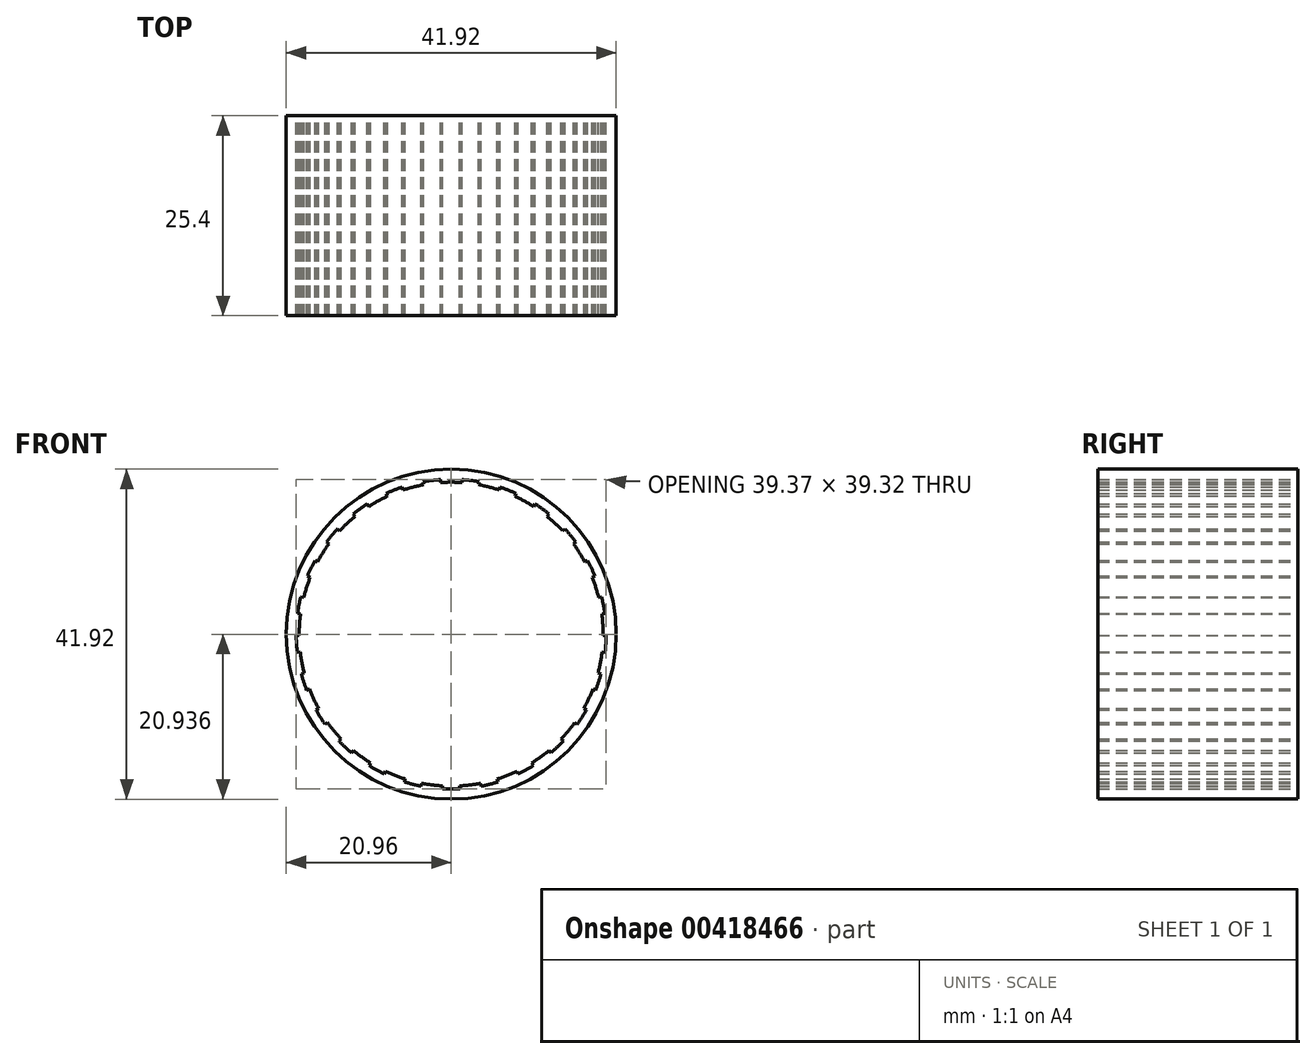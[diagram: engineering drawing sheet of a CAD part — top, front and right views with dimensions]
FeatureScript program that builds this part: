
annotation { "Feature Type Name" : "Feature", "Feature Type Description" : "" }
export const myFeature = defineFeature(function(context is Context, id is Id, definition is map)
    precondition{}
    {
        {
            var Q0;
            Q0=qCreatedBy(makeId("Front.planeOp"),FACE);
            var sketch = newSketch(context, id + "F0", { "sketchPlane" : qUnion([Q0])});
            skCircle(sketch, "E0", {"center": v(0, 0) * mm, "radius": 20.96 * mm});
            skLineSegment(sketch, "E1", {"start": v(1.38, 19.64) * mm, "end": v(1.35, 19.26) * mm});
            skLineSegment(sketch, "E2", {"start": v(-1.38, 19.64) * mm, "end": v(-1.35, 19.26) * mm});
            skArc(sketch, "E3", {"start": v(1.35, 19.26) * mm, "mid": v(0, 19.3) * mm, "end": v(-1.35, 19.26) * mm});
            skPoint(sketch, "E4", {"position": v(1.35, 19.26) * mm});
            skPoint(sketch, "E5", {"position": v(-1.35, 19.26) * mm});
            skPoint(sketch, "E6", {"position": v(0, 19.3) * mm});
            skCircle(sketch, "E7", {"center": v(0, 0) * mm, "radius": 19.69 * mm});
            skArc(sketch, "E8.1.0", {"start": v(-3.48, 18.99) * mm, "mid": v(-4.8, 18.7) * mm, "end": v(-6.1, 18.32) * mm});
            skLineSegment(sketch, "E8.1.1", {"start": v(-3.55, 19.36) * mm, "end": v(-3.48, 18.99) * mm});
            skLineSegment(sketch, "E8.1.2", {"start": v(-6.22, 18.68) * mm, "end": v(-6.1, 18.32) * mm});
            skArc(sketch, "E8.2.0", {"start": v(-8.1, 17.52) * mm, "mid": v(-9.3, 16.92) * mm, "end": v(-10.46, 16.23) * mm});
            skLineSegment(sketch, "E8.2.1", {"start": v(-8.26, 17.87) * mm, "end": v(-8.1, 17.52) * mm});
            skLineSegment(sketch, "E8.2.2", {"start": v(-10.67, 16.55) * mm, "end": v(-10.46, 16.23) * mm});
            skArc(sketch, "E8.3.0", {"start": v(-12.2, 14.96) * mm, "mid": v(-13.21, 14.07) * mm, "end": v(-14.17, 13.11) * mm});
            skLineSegment(sketch, "E8.3.1", {"start": v(-12.44, 15.26) * mm, "end": v(-12.2, 14.96) * mm});
            skLineSegment(sketch, "E8.3.2", {"start": v(-14.44, 13.37) * mm, "end": v(-14.17, 13.11) * mm});
            skArc(sketch, "E8.4.0", {"start": v(-15.54, 11.46) * mm, "mid": v(-16.3, 10.34) * mm, "end": v(-16.98, 9.18) * mm});
            skLineSegment(sketch, "E8.4.1", {"start": v(-15.84, 11.68) * mm, "end": v(-15.54, 11.46) * mm});
            skLineSegment(sketch, "E8.4.2", {"start": v(-17.32, 9.36) * mm, "end": v(-16.98, 9.18) * mm});
            skArc(sketch, "E8.5.0", {"start": v(-17.9, 7.23) * mm, "mid": v(-18.36, 5.97) * mm, "end": v(-18.73, 4.67) * mm});
            skLineSegment(sketch, "E8.5.1", {"start": v(-18.25, 7.38) * mm, "end": v(-17.9, 7.23) * mm});
            skLineSegment(sketch, "E8.5.2", {"start": v(-19.1, 4.76) * mm, "end": v(-18.73, 4.67) * mm});
            skArc(sketch, "E8.6.0", {"start": v(-19.13, 2.56) * mm, "mid": v(-19.27, 1.21) * mm, "end": v(-19.3, -0.14) * mm});
            skLineSegment(sketch, "E8.6.1", {"start": v(-19.51, 2.6) * mm, "end": v(-19.13, 2.56) * mm});
            skLineSegment(sketch, "E8.6.2", {"start": v(-19.68, -0.14) * mm, "end": v(-19.3, -0.14) * mm});
            skArc(sketch, "E8.7.0", {"start": v(-19.17, -2.28) * mm, "mid": v(-18.96, -3.62) * mm, "end": v(-18.66, -4.93) * mm});
            skLineSegment(sketch, "E8.7.1", {"start": v(-19.55, -2.33) * mm, "end": v(-19.17, -2.28) * mm});
            skLineSegment(sketch, "E8.7.2", {"start": v(-19.03, -5.03) * mm, "end": v(-18.66, -4.93) * mm});
            skArc(sketch, "E8.8.0", {"start": v(-18, -6.98) * mm, "mid": v(-17.47, -8.22) * mm, "end": v(-16.85, -9.42) * mm});
            skLineSegment(sketch, "E8.8.1", {"start": v(-18.35, -7.12) * mm, "end": v(-18, -6.98) * mm});
            skLineSegment(sketch, "E8.8.2", {"start": v(-17.18, -9.6) * mm, "end": v(-16.85, -9.42) * mm});
            skArc(sketch, "E8.9.0", {"start": v(-15.7, -11.24) * mm, "mid": v(-14.87, -12.3) * mm, "end": v(-13.98, -13.31) * mm});
            skLineSegment(sketch, "E8.9.1", {"start": v(-16, -11.46) * mm, "end": v(-15.7, -11.24) * mm});
            skLineSegment(sketch, "E8.9.2", {"start": v(-14.25, -13.58) * mm, "end": v(-13.98, -13.31) * mm});
            skArc(sketch, "E8.10.0", {"start": v(-12.4, -14.79) * mm, "mid": v(-11.35, -15.62) * mm, "end": v(-10.23, -16.37) * mm});
            skLineSegment(sketch, "E8.10.1", {"start": v(-12.65, -15.08) * mm, "end": v(-12.4, -14.79) * mm});
            skLineSegment(sketch, "E8.10.2", {"start": v(-10.43, -16.7) * mm, "end": v(-10.23, -16.37) * mm});
            skArc(sketch, "E8.11.0", {"start": v(-8.34, -17.4) * mm, "mid": v(-7.1, -17.95) * mm, "end": v(-5.84, -18.4) * mm});
            skLineSegment(sketch, "E8.11.1", {"start": v(-8.5, -17.75) * mm, "end": v(-8.34, -17.4) * mm});
            skLineSegment(sketch, "E8.11.2", {"start": v(-5.95, -18.76) * mm, "end": v(-5.84, -18.4) * mm});
            skArc(sketch, "E8.12.0", {"start": v(-3.75, -18.94) * mm, "mid": v(-2.42, -19.15) * mm, "end": v(-1.08, -19.27) * mm});
            skLineSegment(sketch, "E8.12.1", {"start": v(-3.83, -19.3) * mm, "end": v(-3.75, -18.94) * mm});
            skLineSegment(sketch, "E8.12.2", {"start": v(-1.1, -19.65) * mm, "end": v(-1.08, -19.27) * mm});
            skArc(sketch, "E8.13.0", {"start": v(1.08, -19.27) * mm, "mid": v(2.42, -19.15) * mm, "end": v(3.75, -18.94) * mm});
            skLineSegment(sketch, "E8.13.1", {"start": v(1.1, -19.65) * mm, "end": v(1.08, -19.27) * mm});
            skLineSegment(sketch, "E8.13.2", {"start": v(3.83, -19.3) * mm, "end": v(3.75, -18.94) * mm});
            skArc(sketch, "E8.14.0", {"start": v(5.84, -18.4) * mm, "mid": v(7.1, -17.95) * mm, "end": v(8.34, -17.4) * mm});
            skLineSegment(sketch, "E8.14.1", {"start": v(5.95, -18.76) * mm, "end": v(5.84, -18.4) * mm});
            skLineSegment(sketch, "E8.14.2", {"start": v(8.5, -17.75) * mm, "end": v(8.34, -17.4) * mm});
            skArc(sketch, "E8.15.0", {"start": v(10.23, -16.37) * mm, "mid": v(11.35, -15.62) * mm, "end": v(12.4, -14.79) * mm});
            skLineSegment(sketch, "E8.15.1", {"start": v(10.43, -16.7) * mm, "end": v(10.23, -16.37) * mm});
            skLineSegment(sketch, "E8.15.2", {"start": v(12.65, -15.08) * mm, "end": v(12.4, -14.79) * mm});
            skArc(sketch, "E8.16.0", {"start": v(13.98, -13.31) * mm, "mid": v(14.87, -12.3) * mm, "end": v(15.7, -11.24) * mm});
            skLineSegment(sketch, "E8.16.1", {"start": v(14.25, -13.58) * mm, "end": v(13.98, -13.31) * mm});
            skLineSegment(sketch, "E8.16.2", {"start": v(16, -11.46) * mm, "end": v(15.7, -11.24) * mm});
            skArc(sketch, "E8.17.0", {"start": v(16.85, -9.42) * mm, "mid": v(17.47, -8.22) * mm, "end": v(18, -6.98) * mm});
            skLineSegment(sketch, "E8.17.1", {"start": v(17.18, -9.6) * mm, "end": v(16.85, -9.42) * mm});
            skLineSegment(sketch, "E8.17.2", {"start": v(18.35, -7.12) * mm, "end": v(18, -6.98) * mm});
            skArc(sketch, "E8.18.0", {"start": v(18.66, -4.93) * mm, "mid": v(18.96, -3.62) * mm, "end": v(19.17, -2.28) * mm});
            skLineSegment(sketch, "E8.18.1", {"start": v(19.03, -5.03) * mm, "end": v(18.66, -4.93) * mm});
            skLineSegment(sketch, "E8.18.2", {"start": v(19.55, -2.33) * mm, "end": v(19.17, -2.28) * mm});
            skArc(sketch, "E8.19.0", {"start": v(19.3, -0.14) * mm, "mid": v(19.27, 1.21) * mm, "end": v(19.13, 2.56) * mm});
            skLineSegment(sketch, "E8.19.1", {"start": v(19.68, -0.14) * mm, "end": v(19.3, -0.14) * mm});
            skLineSegment(sketch, "E8.19.2", {"start": v(19.51, 2.6) * mm, "end": v(19.13, 2.56) * mm});
            skArc(sketch, "E8.20.0", {"start": v(18.73, 4.67) * mm, "mid": v(18.36, 5.97) * mm, "end": v(17.9, 7.23) * mm});
            skLineSegment(sketch, "E8.20.1", {"start": v(19.1, 4.76) * mm, "end": v(18.73, 4.67) * mm});
            skLineSegment(sketch, "E8.20.2", {"start": v(18.25, 7.38) * mm, "end": v(17.9, 7.23) * mm});
            skArc(sketch, "E8.21.0", {"start": v(16.98, 9.18) * mm, "mid": v(16.3, 10.34) * mm, "end": v(15.54, 11.46) * mm});
            skLineSegment(sketch, "E8.21.1", {"start": v(17.32, 9.36) * mm, "end": v(16.98, 9.18) * mm});
            skLineSegment(sketch, "E8.21.2", {"start": v(15.84, 11.68) * mm, "end": v(15.54, 11.46) * mm});
            skArc(sketch, "E8.22.0", {"start": v(14.17, 13.11) * mm, "mid": v(13.21, 14.07) * mm, "end": v(12.2, 14.96) * mm});
            skLineSegment(sketch, "E8.22.1", {"start": v(14.44, 13.37) * mm, "end": v(14.17, 13.11) * mm});
            skLineSegment(sketch, "E8.22.2", {"start": v(12.44, 15.26) * mm, "end": v(12.2, 14.96) * mm});
            skArc(sketch, "E8.23.0", {"start": v(10.46, 16.23) * mm, "mid": v(9.3, 16.92) * mm, "end": v(8.1, 17.52) * mm});
            skLineSegment(sketch, "E8.23.1", {"start": v(10.67, 16.55) * mm, "end": v(10.46, 16.23) * mm});
            skLineSegment(sketch, "E8.23.2", {"start": v(8.26, 17.87) * mm, "end": v(8.1, 17.52) * mm});
            skArc(sketch, "E8.24.0", {"start": v(6.1, 18.32) * mm, "mid": v(4.8, 18.7) * mm, "end": v(3.48, 18.99) * mm});
            skLineSegment(sketch, "E8.24.1", {"start": v(6.22, 18.68) * mm, "end": v(6.1, 18.32) * mm});
            skLineSegment(sketch, "E8.24.2", {"start": v(3.55, 19.36) * mm, "end": v(3.48, 18.99) * mm});
            skSolve(sketch);
        }
        {
            var Q0;
            Q0 = qSketchRegion(id + "F0", true);
            extrude(context, id + "F1", {"entities" : qUnion([Q0]), "depth" : 25.4 * mm});
        }
        {
            var Q0;
            {var subQ0=sQuery(id+"F0.wireOp",EDGE,"E1");Q0=makeQuery(id+"F0.imprint","IMPRINT",FACE,{"disambiguationData":[TD([[makeQuery(id+"F0.imprint","IMPRINT",EDGE,{"derivedFrom":subQ0}),-1.0]])]});}
            var Q1;
            Q1=makeQuery(id+"F0.imprint","IMPRINT",FACE,{"disambiguationData":[TD([[makeQuery(id+"F0.imprint","IMPRINT",EDGE,{"derivedFrom":sQuery(id+"F0.wireOp",EDGE,"E8.1.0")}),-1.0]])]});
            var Q2;
            Q2=makeQuery(id+"F0.imprint","IMPRINT",FACE,{"disambiguationData":[TD([[makeQuery(id+"F0.imprint","IMPRINT",EDGE,{"derivedFrom":sQuery(id+"F0.wireOp",EDGE,"E8.2.0")}),-1.0]])]});
            var Q3;
            Q3=makeQuery(id+"F0.imprint","IMPRINT",FACE,{"disambiguationData":[TD([[makeQuery(id+"F0.imprint","IMPRINT",EDGE,{"derivedFrom":sQuery(id+"F0.wireOp",EDGE,"E8.3.0")}),-1.0]])]});
            var Q4;
            Q4=makeQuery(id+"F0.imprint","IMPRINT",FACE,{"disambiguationData":[TD([[makeQuery(id+"F0.imprint","IMPRINT",EDGE,{"derivedFrom":sQuery(id+"F0.wireOp",EDGE,"E8.4.0")}),-1.0]])]});
            var Q5;
            Q5=makeQuery(id+"F0.imprint","IMPRINT",FACE,{"disambiguationData":[TD([[makeQuery(id+"F0.imprint","IMPRINT",EDGE,{"derivedFrom":sQuery(id+"F0.wireOp",EDGE,"E8.5.0")}),-1.0]])]});
            var Q6;
            Q6=makeQuery(id+"F0.imprint","IMPRINT",FACE,{"disambiguationData":[TD([[makeQuery(id+"F0.imprint","IMPRINT",EDGE,{"derivedFrom":sQuery(id+"F0.wireOp",EDGE,"E8.6.0")}),-1.0]])]});
            var Q7;
            Q7=makeQuery(id+"F0.imprint","IMPRINT",FACE,{"disambiguationData":[TD([[makeQuery(id+"F0.imprint","IMPRINT",EDGE,{"derivedFrom":sQuery(id+"F0.wireOp",EDGE,"E8.7.0")}),-1.0]])]});
            var Q8;
            Q8=makeQuery(id+"F0.imprint","IMPRINT",FACE,{"disambiguationData":[TD([[makeQuery(id+"F0.imprint","IMPRINT",EDGE,{"derivedFrom":sQuery(id+"F0.wireOp",EDGE,"E8.8.0")}),-1.0]])]});
            var Q9;
            Q9=makeQuery(id+"F0.imprint","IMPRINT",FACE,{"disambiguationData":[TD([[makeQuery(id+"F0.imprint","IMPRINT",EDGE,{"derivedFrom":sQuery(id+"F0.wireOp",EDGE,"E8.9.0")}),-1.0]])]});
            var Q10;
            Q10=makeQuery(id+"F0.imprint","IMPRINT",FACE,{"disambiguationData":[TD([[makeQuery(id+"F0.imprint","IMPRINT",EDGE,{"derivedFrom":sQuery(id+"F0.wireOp",EDGE,"E8.10.0")}),-1.0]])]});
            var Q11;
            Q11=makeQuery(id+"F0.imprint","IMPRINT",FACE,{"disambiguationData":[TD([[makeQuery(id+"F0.imprint","IMPRINT",EDGE,{"derivedFrom":sQuery(id+"F0.wireOp",EDGE,"E8.11.0")}),-1.0]])]});
            var Q12;
            Q12=makeQuery(id+"F0.imprint","IMPRINT",FACE,{"disambiguationData":[TD([[makeQuery(id+"F0.imprint","IMPRINT",EDGE,{"derivedFrom":sQuery(id+"F0.wireOp",EDGE,"E8.12.0")}),-1.0]])]});
            var Q13;
            Q13=makeQuery(id+"F0.imprint","IMPRINT",FACE,{"disambiguationData":[TD([[makeQuery(id+"F0.imprint","IMPRINT",EDGE,{"derivedFrom":sQuery(id+"F0.wireOp",EDGE,"E8.13.0")}),-1.0]])]});
            var Q14;
            Q14=makeQuery(id+"F0.imprint","IMPRINT",FACE,{"disambiguationData":[TD([[makeQuery(id+"F0.imprint","IMPRINT",EDGE,{"derivedFrom":sQuery(id+"F0.wireOp",EDGE,"E8.14.0")}),-1.0]])]});
            var Q15;
            Q15=makeQuery(id+"F0.imprint","IMPRINT",FACE,{"disambiguationData":[TD([[makeQuery(id+"F0.imprint","IMPRINT",EDGE,{"derivedFrom":sQuery(id+"F0.wireOp",EDGE,"E8.15.0")}),-1.0]])]});
            var Q16;
            Q16=makeQuery(id+"F0.imprint","IMPRINT",FACE,{"disambiguationData":[TD([[makeQuery(id+"F0.imprint","IMPRINT",EDGE,{"derivedFrom":sQuery(id+"F0.wireOp",EDGE,"E8.16.0")}),-1.0]])]});
            var Q17;
            Q17=makeQuery(id+"F0.imprint","IMPRINT",FACE,{"disambiguationData":[TD([[makeQuery(id+"F0.imprint","IMPRINT",EDGE,{"derivedFrom":sQuery(id+"F0.wireOp",EDGE,"E8.17.0")}),-1.0]])]});
            var Q18;
            Q18=makeQuery(id+"F0.imprint","IMPRINT",FACE,{"disambiguationData":[TD([[makeQuery(id+"F0.imprint","IMPRINT",EDGE,{"derivedFrom":sQuery(id+"F0.wireOp",EDGE,"E8.18.0")}),-1.0]])]});
            var Q19;
            Q19=makeQuery(id+"F0.imprint","IMPRINT",FACE,{"disambiguationData":[TD([[makeQuery(id+"F0.imprint","IMPRINT",EDGE,{"derivedFrom":sQuery(id+"F0.wireOp",EDGE,"E8.19.0")}),-1.0]])]});
            var Q20;
            Q20=makeQuery(id+"F0.imprint","IMPRINT",FACE,{"disambiguationData":[TD([[makeQuery(id+"F0.imprint","IMPRINT",EDGE,{"derivedFrom":sQuery(id+"F0.wireOp",EDGE,"E8.20.0")}),-1.0]])]});
            var Q21;
            Q21=makeQuery(id+"F0.imprint","IMPRINT",FACE,{"disambiguationData":[TD([[makeQuery(id+"F0.imprint","IMPRINT",EDGE,{"derivedFrom":sQuery(id+"F0.wireOp",EDGE,"E8.21.0")}),-1.0]])]});
            var Q22;
            Q22=makeQuery(id+"F0.imprint","IMPRINT",FACE,{"disambiguationData":[TD([[makeQuery(id+"F0.imprint","IMPRINT",EDGE,{"derivedFrom":sQuery(id+"F0.wireOp",EDGE,"E8.22.0")}),-1.0]])]});
            var Q23;
            Q23=makeQuery(id+"F0.imprint","IMPRINT",FACE,{"disambiguationData":[TD([[makeQuery(id+"F0.imprint","IMPRINT",EDGE,{"derivedFrom":sQuery(id+"F0.wireOp",EDGE,"E8.23.0")}),-1.0]])]});
            var Q24;
            Q24=makeQuery(id+"F0.imprint","IMPRINT",FACE,{"disambiguationData":[TD([[makeQuery(id+"F0.imprint","IMPRINT",EDGE,{"derivedFrom":sQuery(id+"F0.wireOp",EDGE,"E8.24.0")}),-1.0]])]});
            extrude(context, id + "F2", {"entities" : qUnion([Q0, Q1, Q2, Q3, Q4, Q5, Q6, Q7, Q8, Q9, Q10, Q11, Q12, Q13, Q14, Q15, Q16, Q17, Q18, Q19, Q20, Q21, Q22, Q23, Q24]), "operationType" : NewBodyOperationType.ADD, "depth" : 25.4 * mm});
        }
    });
